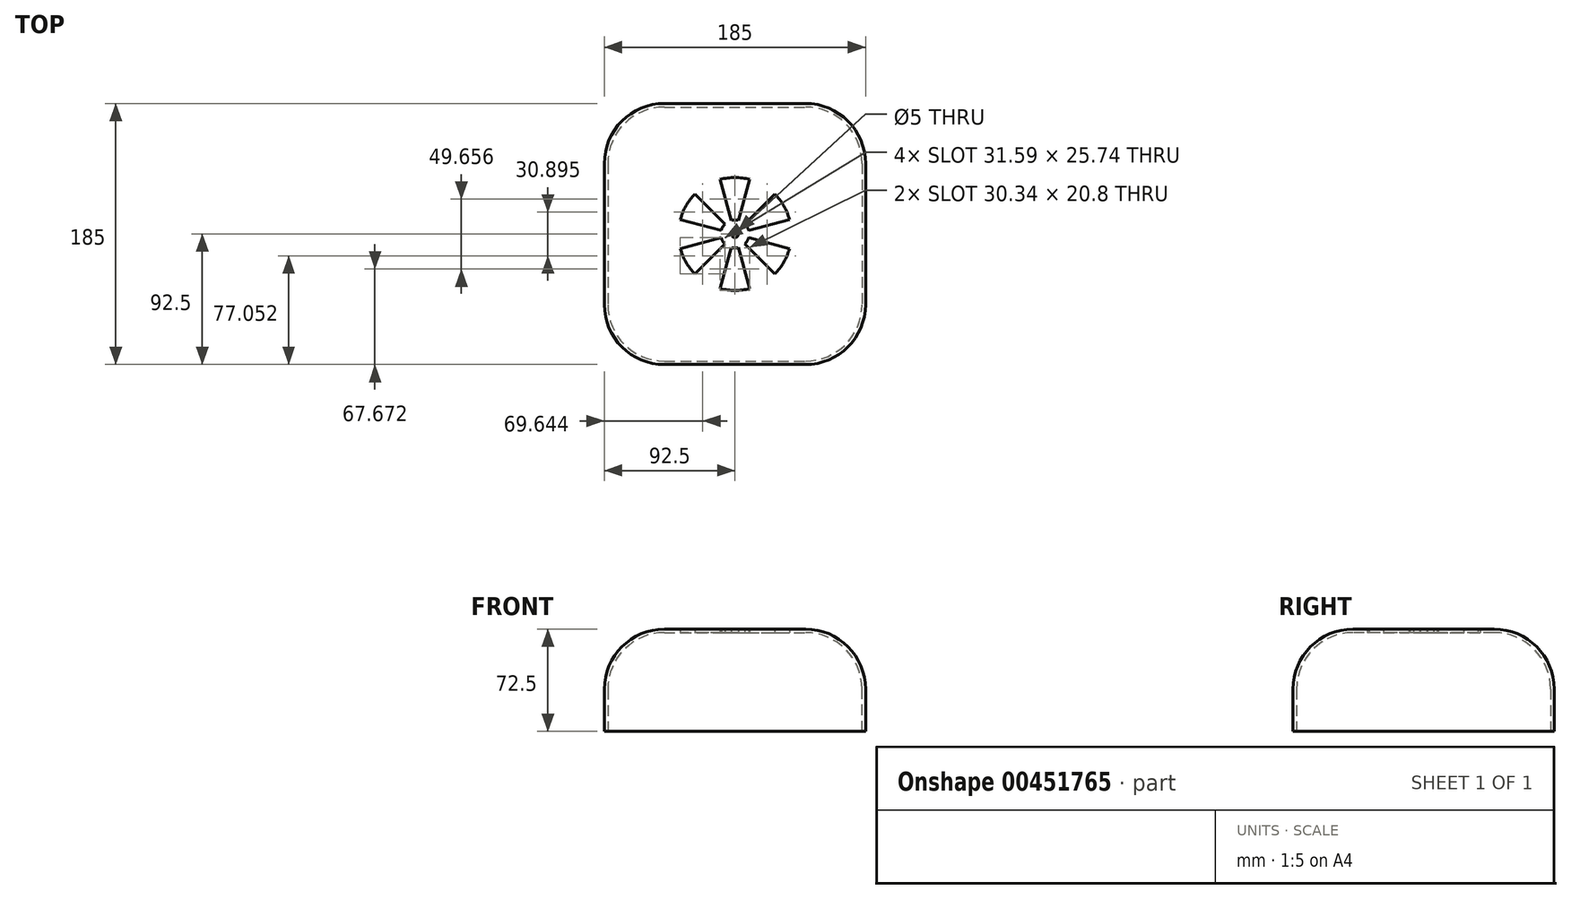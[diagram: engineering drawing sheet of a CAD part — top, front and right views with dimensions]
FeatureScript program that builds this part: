
annotation { "Feature Type Name" : "Feature", "Feature Type Description" : "" }
export const myFeature = defineFeature(function(context is Context, id is Id, definition is map)
    precondition{}
    {
        {
            var Q0;
            Q0=qCreatedBy(makeId("Top.planeOp"),FACE);
            var sketch = newSketch(context, id + "F0", { "sketchPlane" : qUnion([Q0])});
            skPoint(sketch, "E0.middle", {"position": v(0, 0) * mm});
            skCircle(sketch, "E1", {"center": v(0, 0) * mm, "radius": 40 * mm, "construction": true});
            skCircle(sketch, "E2", {"center": v(0, 0) * mm, "radius": 32.5 * mm, "construction": true});
            skCircle(sketch, "E3", {"center": v(0, 0) * mm, "radius": 10 * mm, "construction": true});
            skLineSegment(sketch, "E4", {"start": v(-2.6, 9.66) * mm, "end": v(-10.4, 38.62) * mm});
            skLineSegment(sketch, "E5", {"start": v(2.6, 9.66) * mm, "end": v(10.4, 38.62) * mm});
            skArc(sketch, "E6", {"start": v(-10.4, 38.62) * mm, "mid": v(0, 40) * mm, "end": v(10.4, 38.62) * mm});
            skArc(sketch, "E7", {"start": v(-2.6, 9.66) * mm, "mid": v(0, 10) * mm, "end": v(2.6, 9.66) * mm});
            skLineSegment(sketch, "E8", {"start": v(0, -48.34) * mm, "end": v(0, 48.37) * mm, "construction": true});
            skLineSegment(sketch, "E9.1.0", {"start": v(-7.06, 7.08) * mm, "end": v(-28.25, 28.32) * mm});
            skLineSegment(sketch, "E9.1.1", {"start": v(-9.66, 2.58) * mm, "end": v(-38.65, 10.3) * mm});
            skArc(sketch, "E9.1.2", {"start": v(-38.65, 10.3) * mm, "mid": v(-34.64, 20) * mm, "end": v(-28.25, 28.32) * mm});
            skArc(sketch, "E9.1.3", {"start": v(-9.66, 2.58) * mm, "mid": v(-8.66, 5) * mm, "end": v(-7.06, 7.08) * mm});
            skLineSegment(sketch, "E9.2.0", {"start": v(-9.66, -2.58) * mm, "end": v(-38.65, -10.3) * mm});
            skLineSegment(sketch, "E9.2.1", {"start": v(-7.06, -7.08) * mm, "end": v(-28.25, -28.32) * mm});
            skArc(sketch, "E9.2.2", {"start": v(-28.25, -28.32) * mm, "mid": v(-34.64, -20) * mm, "end": v(-38.65, -10.3) * mm});
            skArc(sketch, "E9.2.3", {"start": v(-7.06, -7.08) * mm, "mid": v(-8.66, -5) * mm, "end": v(-9.66, -2.58) * mm});
            skLineSegment(sketch, "E9.3.0", {"start": v(-2.6, -9.66) * mm, "end": v(-10.4, -38.62) * mm});
            skLineSegment(sketch, "E9.3.1", {"start": v(2.6, -9.66) * mm, "end": v(10.4, -38.62) * mm});
            skArc(sketch, "E9.3.2", {"start": v(10.4, -38.62) * mm, "mid": v(0, -40) * mm, "end": v(-10.4, -38.62) * mm});
            skArc(sketch, "E9.3.3", {"start": v(2.6, -9.66) * mm, "mid": v(0, -10) * mm, "end": v(-2.6, -9.66) * mm});
            skLineSegment(sketch, "E9.4.0", {"start": v(7.06, -7.08) * mm, "end": v(28.25, -28.32) * mm});
            skLineSegment(sketch, "E9.4.1", {"start": v(9.66, -2.58) * mm, "end": v(38.65, -10.3) * mm});
            skArc(sketch, "E9.4.2", {"start": v(38.65, -10.3) * mm, "mid": v(34.64, -20) * mm, "end": v(28.25, -28.32) * mm});
            skArc(sketch, "E9.4.3", {"start": v(9.66, -2.58) * mm, "mid": v(8.66, -5) * mm, "end": v(7.06, -7.08) * mm});
            skLineSegment(sketch, "E9.5.0", {"start": v(9.66, 2.58) * mm, "end": v(38.65, 10.3) * mm});
            skLineSegment(sketch, "E9.5.1", {"start": v(7.06, 7.08) * mm, "end": v(28.25, 28.32) * mm});
            skArc(sketch, "E9.5.2", {"start": v(28.25, 28.32) * mm, "mid": v(34.64, 20) * mm, "end": v(38.65, 10.3) * mm});
            skArc(sketch, "E9.5.3", {"start": v(7.06, 7.08) * mm, "mid": v(8.66, 5) * mm, "end": v(9.66, 2.58) * mm});
            skCircle(sketch, "E10", {"center": v(0, 0) * mm, "radius": 2.5 * mm});
            skSolve(sketch);
        }
        {
            var Q0;
            Q0=qCreatedBy(makeId("Top.planeOp"),FACE);
            cPlane(context, id + "F1", {"entities" : qUnion([Q0]), "cplaneType" : CPlaneType.OFFSET, "offset" : 70 * mm, "oppositeDirection" : true, "width" : 150 * mm, "height" : 150 * mm});
        }
        {
            var Q0;
            Q0=qCreatedBy(id+"F1.planeOp",FACE);
            var sketch = newSketch(context, id + "F2", { "sketchPlane" : qUnion([Q0])});
            skLineSegment(sketch, "E11.bottom", {"start": v(-90, 90) * mm, "end": v(90, 90) * mm});
            skLineSegment(sketch, "E11.top", {"start": v(-90, -90) * mm, "end": v(90, -90) * mm});
            skLineSegment(sketch, "E11.left", {"start": v(-90, 90) * mm, "end": v(-90, -90) * mm});
            skLineSegment(sketch, "E11.right", {"start": v(90, 90) * mm, "end": v(90, -90) * mm});
            skPoint(sketch, "E11.middle", {"position": v(0, 0) * mm});
            skSolve(sketch);
        }
        {
            var Q0;
            Q0=qCreatedBy(makeId("Top.planeOp"),FACE);
            var sketch = newSketch(context, id + "F3", { "sketchPlane" : qUnion([Q0])});
            skLineSegment(sketch, "E12.bottom", {"start": v(90, -90) * mm, "end": v(-90, -90) * mm});
            skLineSegment(sketch, "E12.top", {"start": v(90, 90) * mm, "end": v(-90, 90) * mm});
            skLineSegment(sketch, "E12.left", {"start": v(90, -90) * mm, "end": v(90, 90) * mm});
            skLineSegment(sketch, "E12.right", {"start": v(-90, -90) * mm, "end": v(-90, 90) * mm});
            skPoint(sketch, "E12.middle", {"position": v(0, 0) * mm});
            skSolve(sketch);
        }
        {
            var Q0;
            Q0 = qSketchRegion(id + "F2", true);
            var Q1;
            Q1 = qSketchRegion(id + "F3", true);
            loft(context, id + "F4", {"sheetProfilesArray" : [{ "sheetProfileEntities" : qUnion([Q0]) }, { "sheetProfileEntities" : qUnion([Q1]) }]});
        }
        {
            var Q0;
            Q0=makeQuery(id+"F4.opLoft","MID_CAP_EDGE",EDGE,{"disambiguationData":[OSD([sQuery(id+"F3.wireOp",EDGE,"E12.bottom"),sQuery(id+"F3.wireOp",EDGE,"E12.top"),sQuery(id+"F3.wireOp",EDGE,"E12.left")])],"capPos":1.0});
            var Q1;
            Q1=makeQuery(id+"F4.opLoft","MID_CAP_EDGE",EDGE,{"disambiguationData":[OSD([sQuery(id+"F3.wireOp",EDGE,"E12.bottom"),sQuery(id+"F3.wireOp",EDGE,"E12.left"),sQuery(id+"F3.wireOp",EDGE,"E12.right")])],"capPos":1.0});
            var Q2;
            Q2=makeQuery(id+"F4.opLoft","MID_CAP_EDGE",EDGE,{"disambiguationData":[OSD([sQuery(id+"F3.wireOp",EDGE,"E12.bottom"),sQuery(id+"F3.wireOp",EDGE,"E12.top"),sQuery(id+"F3.wireOp",EDGE,"E12.right")])],"capPos":1.0});
            var Q3;
            Q3=makeQuery(id+"F4.opLoft","MID_CAP_EDGE",EDGE,{"disambiguationData":[OSD([sQuery(id+"F3.wireOp",EDGE,"E12.top"),sQuery(id+"F3.wireOp",EDGE,"E12.left"),sQuery(id+"F3.wireOp",EDGE,"E12.right")])],"capPos":1.0});
            fillet(context, id + "F5", {"entities" : qUnion([Q0, Q1, Q2, Q3]), "radius" : 40 * mm, "tangentPropagation" : true, "allowEdgeOverflow" : false});
        }
        {
            var Q0;
            Q0=makeQuery(id+"F4.opLoft","SWEPT_EDGE",EDGE,{"disambiguationData":[OSD([sQuery(id+"F2.wireOp",EDGE,"E11.top"),sQuery(id+"F2.wireOp",EDGE,"E11.right"),sQuery(id+"F3.wireOp",EDGE,"E12.bottom"),sQuery(id+"F3.wireOp",EDGE,"E12.left")])]});
            var Q1;
            {var subQ0=sQuery(id+"F3.wireOp",EDGE,"E12.left");var subQ1=sQuery(id+"F3.wireOp",EDGE,"E12.bottom");Q1=makeQuery(id+"F5.opFillet","BLEND_EDGE",EDGE,{"blendedFrom":[makeQuery(id+"F4.opLoft","MID_CAP_EDGE",EDGE,{"disambiguationData":[OSD([subQ1,subQ0,sQuery(id+"F3.wireOp",EDGE,"E12.right")])],"capPos":1.0}),makeQuery(id+"F4.opLoft","MID_CAP_EDGE",EDGE,{"disambiguationData":[OSD([subQ1,sQuery(id+"F3.wireOp",EDGE,"E12.top"),subQ0])],"capPos":1.0})],"blendedInto":[]});}
            var Q2;
            {var subQ0=sQuery(id+"F3.wireOp",EDGE,"E12.left");var subQ1=sQuery(id+"F3.wireOp",EDGE,"E12.top");Q2=makeQuery(id+"F5.opFillet","BLEND_EDGE",EDGE,{"blendedFrom":[makeQuery(id+"F4.opLoft","MID_CAP_EDGE",EDGE,{"disambiguationData":[OSD([sQuery(id+"F3.wireOp",EDGE,"E12.bottom"),subQ1,subQ0])],"capPos":1.0}),makeQuery(id+"F4.opLoft","MID_CAP_EDGE",EDGE,{"disambiguationData":[OSD([subQ1,subQ0,sQuery(id+"F3.wireOp",EDGE,"E12.right")])],"capPos":1.0})],"blendedInto":[]});}
            var Q3;
            Q3=makeQuery(id+"F4.opLoft","SWEPT_EDGE",EDGE,{"disambiguationData":[OSD([sQuery(id+"F2.wireOp",EDGE,"E11.bottom"),sQuery(id+"F2.wireOp",EDGE,"E11.right"),sQuery(id+"F3.wireOp",EDGE,"E12.top"),sQuery(id+"F3.wireOp",EDGE,"E12.left")])]});
            var Q4;
            {var subQ0=sQuery(id+"F3.wireOp",EDGE,"E12.right");var subQ1=sQuery(id+"F3.wireOp",EDGE,"E12.top");Q4=makeQuery(id+"F5.opFillet","BLEND_EDGE",EDGE,{"blendedFrom":[makeQuery(id+"F4.opLoft","MID_CAP_EDGE",EDGE,{"disambiguationData":[OSD([sQuery(id+"F3.wireOp",EDGE,"E12.bottom"),subQ1,subQ0])],"capPos":1.0}),makeQuery(id+"F4.opLoft","MID_CAP_EDGE",EDGE,{"disambiguationData":[OSD([subQ1,sQuery(id+"F3.wireOp",EDGE,"E12.left"),subQ0])],"capPos":1.0})],"blendedInto":[]});}
            var Q5;
            Q5=makeQuery(id+"F4.opLoft","SWEPT_EDGE",EDGE,{"disambiguationData":[OSD([sQuery(id+"F2.wireOp",EDGE,"E11.bottom"),sQuery(id+"F2.wireOp",EDGE,"E11.left"),sQuery(id+"F3.wireOp",EDGE,"E12.top"),sQuery(id+"F3.wireOp",EDGE,"E12.right")])]});
            var Q6;
            {var subQ0=sQuery(id+"F3.wireOp",EDGE,"E12.right");var subQ1=sQuery(id+"F3.wireOp",EDGE,"E12.bottom");Q6=makeQuery(id+"F5.opFillet","BLEND_EDGE",EDGE,{"blendedFrom":[makeQuery(id+"F4.opLoft","MID_CAP_EDGE",EDGE,{"disambiguationData":[OSD([subQ1,sQuery(id+"F3.wireOp",EDGE,"E12.left"),subQ0])],"capPos":1.0}),makeQuery(id+"F4.opLoft","MID_CAP_EDGE",EDGE,{"disambiguationData":[OSD([subQ1,sQuery(id+"F3.wireOp",EDGE,"E12.top"),subQ0])],"capPos":1.0})],"blendedInto":[]});}
            var Q7;
            Q7=makeQuery(id+"F4.opLoft","SWEPT_EDGE",EDGE,{"disambiguationData":[OSD([sQuery(id+"F2.wireOp",EDGE,"E11.top"),sQuery(id+"F2.wireOp",EDGE,"E11.left"),sQuery(id+"F3.wireOp",EDGE,"E12.bottom"),sQuery(id+"F3.wireOp",EDGE,"E12.right")])]});
            fillet(context, id + "F6", {"entities" : qUnion([Q0, Q1, Q2, Q3, Q4, Q5, Q6, Q7]), "radius" : 40 * mm, "tangentPropagation" : true, "allowEdgeOverflow" : false});
        }
        {
            var Q0;
            Q0=makeQuery(id+"F4.opLoft","CAP_FACE",FACE,{"disambiguationData":[OSD([makeQuery(id+"F2.imprint","IMPRINT",FACE,{"disambiguationData":[TD([[makeQuery(id+"F2.imprint","IMPRINT",EDGE,{"derivedFrom":sQuery(id+"F2.wireOp",EDGE,"E11.bottom")}),-1.0]])]})])],"isStart":true});
            shell(context, id + "F7", {"entities" : qUnion([Q0]), "thickness" : 2.5 * mm, "oppositeDirection" : true});
        }
        {
            var Q0;
            Q0 = qSketchRegion(id + "F0", true);
            extrude(context, id + "F8", {"entities" : qUnion([Q0]), "operationType" : NewBodyOperationType.REMOVE, "endBound" : BoundingType.THROUGH_ALL, "depth" : 25 * mm, "offsetDistance" : 25 * mm});
        }
    });
